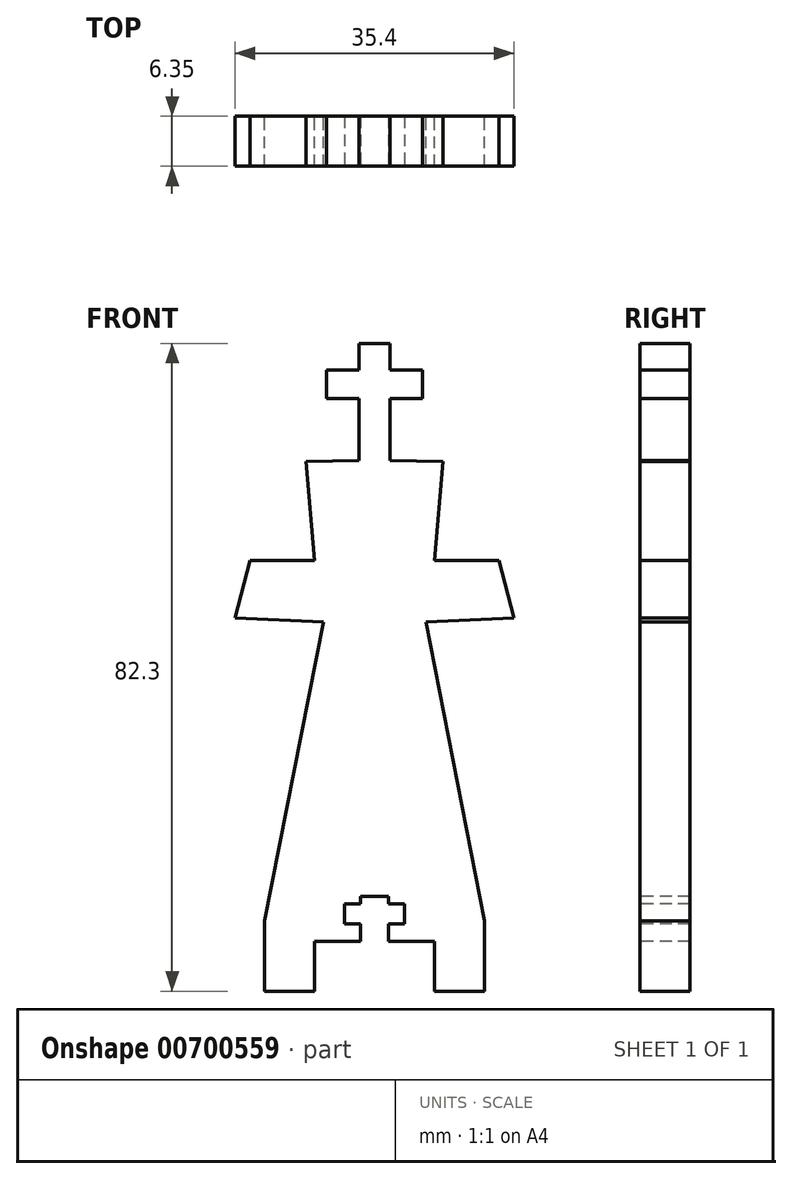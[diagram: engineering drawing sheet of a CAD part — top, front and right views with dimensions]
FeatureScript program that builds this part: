
annotation { "Feature Type Name" : "Feature", "Feature Type Description" : "" }
export const myFeature = defineFeature(function(context is Context, id is Id, definition is map)
    precondition{}
    {
        {
            var Q0;
            Q0=qCreatedBy(makeId("Front.planeOp"),FACE);
            var sketch = newSketch(context, id + "F0", { "sketchPlane" : qUnion([Q0])});
            skLineSegment(sketch, "E0", {"start": v(-13.97, 0) * mm, "end": v(-13.97, -6.35) * mm});
            skLineSegment(sketch, "E1", {"start": v(-13.97, -6.35) * mm, "end": v(-7.62, -6.35) * mm});
            skLineSegment(sketch, "E2", {"start": v(-7.62, -6.35) * mm, "end": v(-7.62, 0) * mm});
            skLineSegment(sketch, "E3", {"start": v(-7.62, 0) * mm, "end": v(7.62, 0) * mm});
            skLineSegment(sketch, "E4", {"start": v(7.62, 0) * mm, "end": v(7.62, -6.35) * mm});
            skLineSegment(sketch, "E5", {"start": v(7.62, -6.35) * mm, "end": v(13.97, -6.35) * mm});
            skLineSegment(sketch, "E6", {"start": v(13.97, -6.35) * mm, "end": v(13.97, 0) * mm});
            skLineSegment(sketch, "E7", {"start": v(-13.97, 0) * mm, "end": v(-13.97, 0) * mm});
            skLineSegment(sketch, "E8", {"start": v(-13.97, 0) * mm, "end": v(-13.97, 2.61) * mm});
            skLineSegment(sketch, "E9", {"start": v(-13.97, 2.61) * mm, "end": v(-6.5, 40.55) * mm});
            skLineSegment(sketch, "E10", {"start": v(-6.5, 40.55) * mm, "end": v(-17.7, 41.05) * mm});
            skLineSegment(sketch, "E11", {"start": v(-17.7, 41.05) * mm, "end": v(-15.84, 48.39) * mm});
            skLineSegment(sketch, "E12", {"start": v(-15.84, 48.39) * mm, "end": v(-7.6, 48.39) * mm});
            skLineSegment(sketch, "E13", {"start": v(-7.6, 48.39) * mm, "end": v(-8.7, 60.93) * mm});
            skLineSegment(sketch, "E14", {"start": v(-8.7, 60.93) * mm, "end": v(-1.96, 61.08) * mm});
            skLineSegment(sketch, "E15", {"start": v(-1.96, 61.08) * mm, "end": v(-1.96, 68.93) * mm});
            skLineSegment(sketch, "E16", {"start": v(-1.96, 68.93) * mm, "end": v(-6.1, 68.93) * mm});
            skLineSegment(sketch, "E17", {"start": v(-6.1, 68.93) * mm, "end": v(-6.1, 72.56) * mm});
            skLineSegment(sketch, "E18", {"start": v(-6.1, 72.56) * mm, "end": v(-1.96, 72.56) * mm});
            skLineSegment(sketch, "E19", {"start": v(-1.96, 72.56) * mm, "end": v(-1.96, 75.95) * mm});
            skLineSegment(sketch, "E20.MirrorCS", {"start": v(1.96, 72.56) * mm, "end": v(1.96, 75.95) * mm});
            skLineSegment(sketch, "E21.MirrorCS", {"start": v(1.96, 61.08) * mm, "end": v(1.96, 68.93) * mm});
            skLineSegment(sketch, "E22.MirrorCS", {"start": v(1.96, 68.93) * mm, "end": v(6.1, 68.93) * mm});
            skLineSegment(sketch, "E23.MirrorCS", {"start": v(6.1, 68.93) * mm, "end": v(6.1, 72.56) * mm});
            skLineSegment(sketch, "E24.MirrorCS", {"start": v(6.1, 72.56) * mm, "end": v(1.96, 72.56) * mm});
            skLineSegment(sketch, "E25.MirrorCS", {"start": v(17.7, 41.05) * mm, "end": v(15.84, 48.39) * mm});
            skLineSegment(sketch, "E26.MirrorCS", {"start": v(8.7, 60.93) * mm, "end": v(1.96, 61.08) * mm});
            skLineSegment(sketch, "E27.MirrorCS", {"start": v(7.6, 48.39) * mm, "end": v(8.7, 60.93) * mm});
            skLineSegment(sketch, "E28.MirrorCS", {"start": v(15.84, 48.39) * mm, "end": v(7.6, 48.39) * mm});
            skLineSegment(sketch, "E29.MirrorCS", {"start": v(6.5, 40.55) * mm, "end": v(17.7, 41.05) * mm});
            skLineSegment(sketch, "E30.MirrorCS", {"start": v(13.97, 2.61) * mm, "end": v(6.5, 40.55) * mm});
            skLineSegment(sketch, "E31", {"start": v(13.97, 2.61) * mm, "end": v(13.97, 0) * mm});
            skLineSegment(sketch, "E32", {"start": v(13.97, 0) * mm, "end": v(13.97, 0) * mm});
            skLineSegment(sketch, "E33", {"start": v(-1.96, 75.95) * mm, "end": v(1.96, 75.95) * mm});
            skSolve(sketch);
        }
        {
            var Q0;
            Q0 = qSketchRegion(id + "F0", true);
            extrude(context, id + "F1", {"entities" : qUnion([Q0]), "depth" : 6.35 * mm, "offsetDistance" : 25.4 * mm});
        }
        {
            var Q0;
            Q0=makeQuery(id+"F1.opExtrude","CAP_FACE",FACE,{"disambiguationData":[OSD([sQuery(id+"F0.wireOp",EDGE,"E0"),sQuery(id+"F0.wireOp",EDGE,"E1"),sQuery(id+"F0.wireOp",EDGE,"E2"),sQuery(id+"F0.wireOp",EDGE,"E3"),sQuery(id+"F0.wireOp",EDGE,"E4"),sQuery(id+"F0.wireOp",EDGE,"E5"),sQuery(id+"F0.wireOp",EDGE,"E6"),sQuery(id+"F0.wireOp",EDGE,"E8"),sQuery(id+"F0.wireOp",EDGE,"E9"),sQuery(id+"F0.wireOp",EDGE,"E10"),sQuery(id+"F0.wireOp",EDGE,"E11"),sQuery(id+"F0.wireOp",EDGE,"E12"),sQuery(id+"F0.wireOp",EDGE,"E13"),sQuery(id+"F0.wireOp",EDGE,"E14"),sQuery(id+"F0.wireOp",EDGE,"E15"),sQuery(id+"F0.wireOp",EDGE,"E16"),sQuery(id+"F0.wireOp",EDGE,"E17"),sQuery(id+"F0.wireOp",EDGE,"E18"),sQuery(id+"F0.wireOp",EDGE,"E19"),sQuery(id+"F0.wireOp",EDGE,"E20.MirrorCS"),sQuery(id+"F0.wireOp",EDGE,"E21.MirrorCS"),sQuery(id+"F0.wireOp",EDGE,"E22.MirrorCS"),sQuery(id+"F0.wireOp",EDGE,"E23.MirrorCS"),sQuery(id+"F0.wireOp",EDGE,"E24.MirrorCS"),sQuery(id+"F0.wireOp",EDGE,"E25.MirrorCS"),sQuery(id+"F0.wireOp",EDGE,"E26.MirrorCS"),sQuery(id+"F0.wireOp",EDGE,"E27.MirrorCS"),sQuery(id+"F0.wireOp",EDGE,"E28.MirrorCS"),sQuery(id+"F0.wireOp",EDGE,"E29.MirrorCS"),sQuery(id+"F0.wireOp",EDGE,"E30.MirrorCS"),sQuery(id+"F0.wireOp",EDGE,"E31"),sQuery(id+"F0.wireOp",EDGE,"E33")])],"isStart":false});
            var sketch = newSketch(context, id + "F2", { "sketchPlane" : qUnion([Q0])});
            skLineSegment(sketch, "E34.bottom", {"start": v(-1.78, 5.72) * mm, "end": v(1.78, 5.72) * mm});
            skLineSegment(sketch, "E34.left", {"start": v(-1.78, 5.72) * mm, "end": v(-1.78, 4.76) * mm});
            skLineSegment(sketch, "E35", {"start": v(0, 5.71) * mm, "end": v(0, 9.6) * mm, "construction": true});
            skLineSegment(sketch, "E36.bottom", {"start": v(-1.78, 4.76) * mm, "end": v(-3.8, 4.76) * mm});
            skLineSegment(sketch, "E36.top", {"start": v(-1.78, 2.22) * mm, "end": v(-3.8, 2.22) * mm});
            skLineSegment(sketch, "E36.right", {"start": v(-3.8, 4.76) * mm, "end": v(-3.8, 2.22) * mm});
            skLineSegment(sketch, "E37.top", {"start": v(-1.78, 0) * mm, "end": v(1.78, 0) * mm});
            skLineSegment(sketch, "E37.left", {"start": v(-1.78, 2.22) * mm, "end": v(-1.78, 0) * mm});
            skLineSegment(sketch, "E38.MirrorCS", {"start": v(0, 5.72) * mm, "end": v(0, 9.6) * mm, "construction": true});
            skLineSegment(sketch, "E39.MirrorCS", {"start": v(3.81, 4.76) * mm, "end": v(3.81, 2.22) * mm});
            skLineSegment(sketch, "E40.MirrorCS", {"start": v(1.78, 5.72) * mm, "end": v(1.78, 4.76) * mm});
            skLineSegment(sketch, "E41.MirrorCS", {"start": v(1.78, 2.22) * mm, "end": v(1.78, 0) * mm});
            skLineSegment(sketch, "E42.MirrorCS", {"start": v(1.78, 4.76) * mm, "end": v(3.81, 4.76) * mm});
            skLineSegment(sketch, "E43.MirrorCS", {"start": v(1.78, 0) * mm, "end": v(-1.78, 0) * mm});
            skLineSegment(sketch, "E44.MirrorCS", {"start": v(1.78, 2.22) * mm, "end": v(3.81, 2.22) * mm});
            skLineSegment(sketch, "E45.MirrorCS", {"start": v(1.78, 5.72) * mm, "end": v(-1.78, 5.72) * mm});
            skSolve(sketch);
        }
        {
            var Q0;
            Q0 = qSketchRegion(id + "F2", true);
            extrude(context, id + "F3", {"entities" : qUnion([Q0]), "operationType" : NewBodyOperationType.REMOVE, "oppositeDirection" : true, "depth" : 25.4 * mm, "offsetDistance" : 25.4 * mm});
        }
    });
